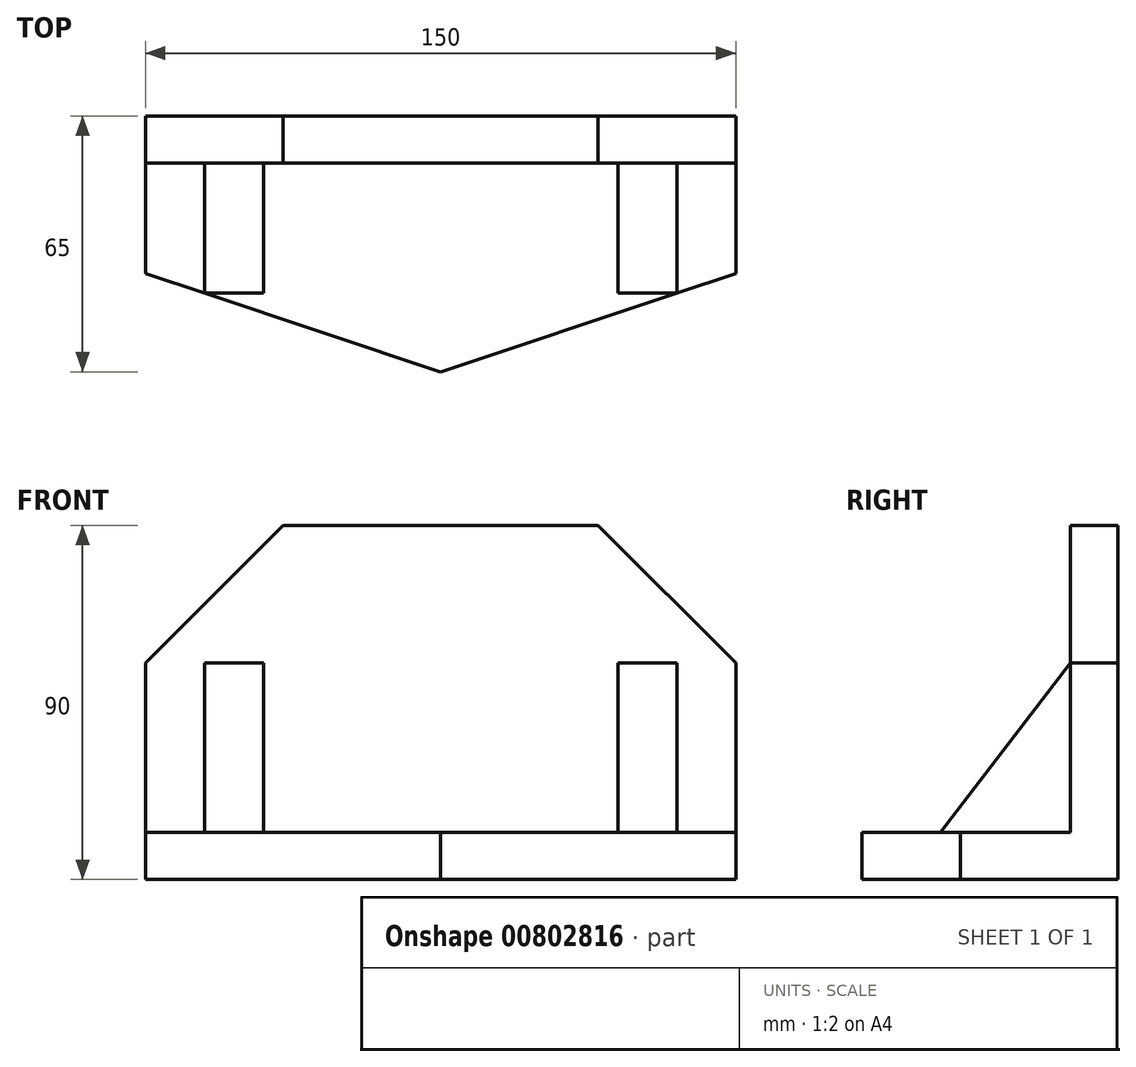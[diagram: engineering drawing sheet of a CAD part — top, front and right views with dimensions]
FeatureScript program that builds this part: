
annotation { "Feature Type Name" : "Feature", "Feature Type Description" : "" }
export const myFeature = defineFeature(function(context is Context, id is Id, definition is map)
    precondition{}
    {
        {
            var Q0;
            Q0=qCreatedBy(makeId("Top.planeOp"),FACE);
            var sketch = newSketch(context, id + "F0", { "sketchPlane" : qUnion([Q0])});
            skLineSegment(sketch, "E0.bottom", {"start": v(-75, 32.5) * mm, "end": v(75, 32.5) * mm});
            skLineSegment(sketch, "E0.top", {"start": v(-75, -32.5) * mm, "end": v(75, -32.5) * mm});
            skLineSegment(sketch, "E0.left", {"start": v(-75, 32.5) * mm, "end": v(-75, -32.5) * mm});
            skLineSegment(sketch, "E0.right", {"start": v(75, 32.5) * mm, "end": v(75, -32.5) * mm});
            skLineSegment(sketch, "E1", {"start": v(-75, 20.5) * mm, "end": v(75, 20.5) * mm});
            skLineSegment(sketch, "E2", {"start": v(0, -32.5) * mm, "end": v(-75, -7.5) * mm});
            skLineSegment(sketch, "E3", {"start": v(0, -32.5) * mm, "end": v(75, -7.5) * mm});
            skSolve(sketch);
        }
        {
            var Q0;
            {var subQ1=sQuery(id+"F0.wireOp",EDGE,"E1");Q0=makeQuery(id+"F0.imprint","IMPRINT",FACE,{"disambiguationData":[TD([[makeQuery(id+"F0.imprint","IMPRINT",EDGE,{"derivedFrom":subQ1}),-1.0]])]});}
            extrude(context, id + "F1", {"entities" : qUnion([Q0]), "depth" : 12 * mm, "offsetDistance" : 25 * mm});
        }
        {
            var Q0;
            Q0=qCreatedBy(makeId("Top.planeOp"),FACE);
            var sketch = newSketch(context, id + "F2", { "sketchPlane" : qUnion([Q0])});
            skLineSegment(sketch, "E4.bottom", {"start": v(-75, 20.5) * mm, "end": v(75, 20.5) * mm});
            skLineSegment(sketch, "E4.top", {"start": v(-75, 32.5) * mm, "end": v(75, 32.5) * mm});
            skLineSegment(sketch, "E4.left", {"start": v(-75, 20.5) * mm, "end": v(-75, 32.5) * mm});
            skLineSegment(sketch, "E4.right", {"start": v(75, 20.5) * mm, "end": v(75, 32.5) * mm});
            skSolve(sketch);
        }
        {
            var Q0;
            Q0 = qSketchRegion(id + "F2", true);
            extrude(context, id + "F3", {"entities" : qUnion([Q0]), "operationType" : NewBodyOperationType.ADD, "depth" : 90 * mm, "offsetDistance" : 25 * mm});
        }
        {
            var Q0;
            Q0=makeQuery(id+"F3.opExtrude","CAP_EDGE",EDGE,{"disambiguationData":[OSD([sQuery(id+"F2.wireOp",EDGE,"E4.left")])],"isStart":false});
            var Q1;
            Q1=makeQuery(id+"F3.opExtrude","CAP_EDGE",EDGE,{"disambiguationData":[OSD([sQuery(id+"F2.wireOp",EDGE,"E4.right")])],"isStart":false});
            chamfer(context, id + "F4", {"entities" : qUnion([Q0, Q1]), "chamferType" : ChamferType.TWO_OFFSETS, "width1" : 35 * mm, "oppositeDirection" : false, "width2" : 35 * mm, "tangentPropagation" : true});
        }
        {
            var Q0;
            Q0=qCreatedBy(makeId("Top.planeOp"),FACE);
            var sketch = newSketch(context, id + "F5", { "sketchPlane" : qUnion([Q0])});
            skLineSegment(sketch, "E5.bottom", {"start": v(-60, 20.5) * mm, "end": v(-45, 20.5) * mm});
            skLineSegment(sketch, "E5.top", {"start": v(-60, -12.5) * mm, "end": v(-45, -12.5) * mm});
            skLineSegment(sketch, "E5.left", {"start": v(-60, 20.5) * mm, "end": v(-60, -12.5) * mm});
            skLineSegment(sketch, "E5.right", {"start": v(-45, 20.5) * mm, "end": v(-45, -12.5) * mm});
            skLineSegment(sketch, "E6.MirrorCS", {"start": v(45, 20.5) * mm, "end": v(45, -12.5) * mm});
            skLineSegment(sketch, "E7.MirrorCS", {"start": v(60, -12.5) * mm, "end": v(45, -12.5) * mm});
            skLineSegment(sketch, "E8.MirrorCS", {"start": v(60, 20.5) * mm, "end": v(60, -12.5) * mm});
            skLineSegment(sketch, "E9.MirrorCS", {"start": v(60, 20.5) * mm, "end": v(45, 20.5) * mm});
            skSolve(sketch);
        }
        {
            var Q0;
            Q0 = qSketchRegion(id + "F5", true);
            extrude(context, id + "F6", {"entities" : qUnion([Q0]), "operationType" : NewBodyOperationType.ADD, "depth" : 55 * mm, "offsetDistance" : 25 * mm});
        }
        {
            var Q0;
            Q0=qCreatedBy(makeId("Right.planeOp"),FACE);
            var sketch = newSketch(context, id + "F7", { "sketchPlane" : qUnion([Q0])});
            skLineSegment(sketch, "E10", {"start": v(20.5, 55) * mm, "end": v(-12.5, 12) * mm});
            skLineSegment(sketch, "E11", {"start": v(-12.5, 12) * mm, "end": v(-12.5, 55) * mm});
            skLineSegment(sketch, "E12", {"start": v(-12.5, 55) * mm, "end": v(20.5, 55) * mm});
            skSolve(sketch);
        }
        {
            var Q0;
            Q0 = qSketchRegion(id + "F7", true);
            extrude(context, id + "F8", {"entities" : qUnion([Q0]), "operationType" : NewBodyOperationType.REMOVE, "oppositeDirection" : true, "depth" : 60 * mm, "offsetDistance" : 25 * mm, "hasSecondDirection" : true, "secondDirectionOppositeDirection" : false, "secondDirectionDepth" : 60 * mm});
        }
    });
